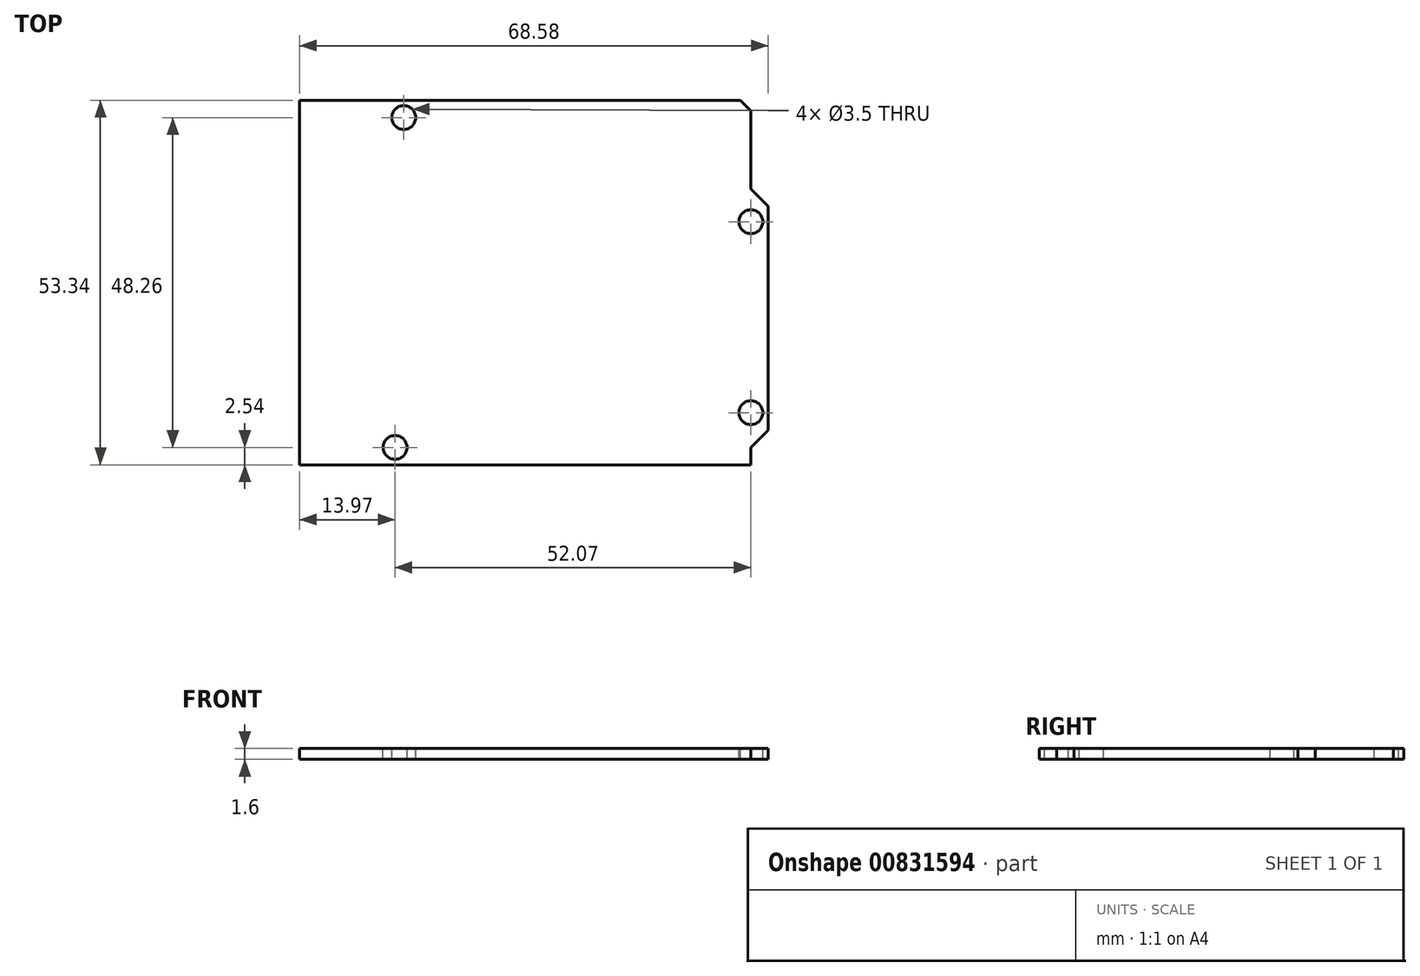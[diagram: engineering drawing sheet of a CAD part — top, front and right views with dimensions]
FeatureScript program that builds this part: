
annotation { "Feature Type Name" : "Feature", "Feature Type Description" : "" }
export const myFeature = defineFeature(function(context is Context, id is Id, definition is map)
    precondition{}
    {
        {
            var Q0;
            Q0=qCreatedBy(makeId("Top.planeOp"),FACE);
            var sketch = newSketch(context, id + "F0", { "sketchPlane" : qUnion([Q0])});
            skLineSegment(sketch, "E0", {"start": v(0, 0) * mm, "end": v(66.04, 0) * mm});
            skLineSegment(sketch, "E1", {"start": v(66.04, 0) * mm, "end": v(66.04, 2.54) * mm});
            skLineSegment(sketch, "E2", {"start": v(66.04, 2.54) * mm, "end": v(68.58, 5.08) * mm});
            skLineSegment(sketch, "E3", {"start": v(68.58, 5.08) * mm, "end": v(68.58, 37.85) * mm});
            skLineSegment(sketch, "E4", {"start": v(68.58, 37.85) * mm, "end": v(66.04, 40.39) * mm});
            skLineSegment(sketch, "E5", {"start": v(66.04, 40.39) * mm, "end": v(66.04, 51.82) * mm});
            skLineSegment(sketch, "E6", {"start": v(66.04, 51.82) * mm, "end": v(64.52, 53.34) * mm});
            skLineSegment(sketch, "E7", {"start": v(64.52, 53.34) * mm, "end": v(0, 53.34) * mm});
            skLineSegment(sketch, "E8", {"start": v(0, 53.34) * mm, "end": v(0, 0) * mm});
            skCircle(sketch, "E9", {"center": v(13.97, 2.54) * mm, "radius": 1.75 * mm});
            skCircle(sketch, "E10", {"center": v(15.24, 50.8) * mm, "radius": 1.75 * mm});
            skCircle(sketch, "E11", {"center": v(66.04, 35.56) * mm, "radius": 1.75 * mm});
            skCircle(sketch, "E12", {"center": v(66.04, 7.62) * mm, "radius": 1.75 * mm});
            skLineSegment(sketch, "E13.bottom", {"start": v(11.43, 12.06) * mm, "end": v(-1.9, 12.06) * mm});
            skLineSegment(sketch, "E13.top", {"start": v(11.43, 3.17) * mm, "end": v(-1.9, 3.17) * mm});
            skLineSegment(sketch, "E13.left", {"start": v(11.43, 12.06) * mm, "end": v(11.43, 3.17) * mm});
            skLineSegment(sketch, "E13.right", {"start": v(-1.9, 12.06) * mm, "end": v(-1.9, 3.17) * mm});
            skPoint(sketch, "E13.middle", {"position": v(4.76, 7.62) * mm});
            skLineSegment(sketch, "E14.bottom", {"start": v(-6.35, 45.09) * mm, "end": v(9.52, 45.09) * mm});
            skLineSegment(sketch, "E14.top", {"start": v(-6.35, 32.39) * mm, "end": v(9.53, 32.39) * mm});
            skLineSegment(sketch, "E14.left", {"start": v(-6.35, 45.09) * mm, "end": v(-6.35, 32.39) * mm});
            skLineSegment(sketch, "E14.right", {"start": v(9.52, 45.09) * mm, "end": v(9.52, 32.39) * mm});
            skPoint(sketch, "E14.middle", {"position": v(1.59, 38.74) * mm});
            skSolve(sketch);
        }
        {
            var Q0;
            {var subQ9=sQuery(id+"F0.wireOp",EDGE,"E0");Q0=makeQuery(id+"F0.imprint","IMPRINT",FACE,{"disambiguationData":[TD([[makeQuery(id+"F0.imprint","IMPRINT",EDGE,{"derivedFrom":subQ9}),1.0]])]});}
            var Q1;
            {var subQ5=sQuery(id+"F0.wireOp",EDGE,"E14.right");Q1=makeQuery(id+"F0.imprint","IMPRINT",FACE,{"disambiguationData":[TD([[makeQuery(id+"F0.imprint","IMPRINT",EDGE,{"derivedFrom":subQ5}),-1.0]])]});}
            var Q2;
            {var subQ5=sQuery(id+"F0.wireOp",EDGE,"E13.left");Q2=makeQuery(id+"F0.imprint","IMPRINT",FACE,{"disambiguationData":[TD([[makeQuery(id+"F0.imprint","IMPRINT",EDGE,{"derivedFrom":subQ5}),-1.0]])]});}
            extrude(context, id + "F1", {"entities" : qUnion([Q0, Q1, Q2]), "oppositeDirection" : true, "depth" : 1.6 * mm, "offsetDistance" : 25 * mm});
        }
    });
